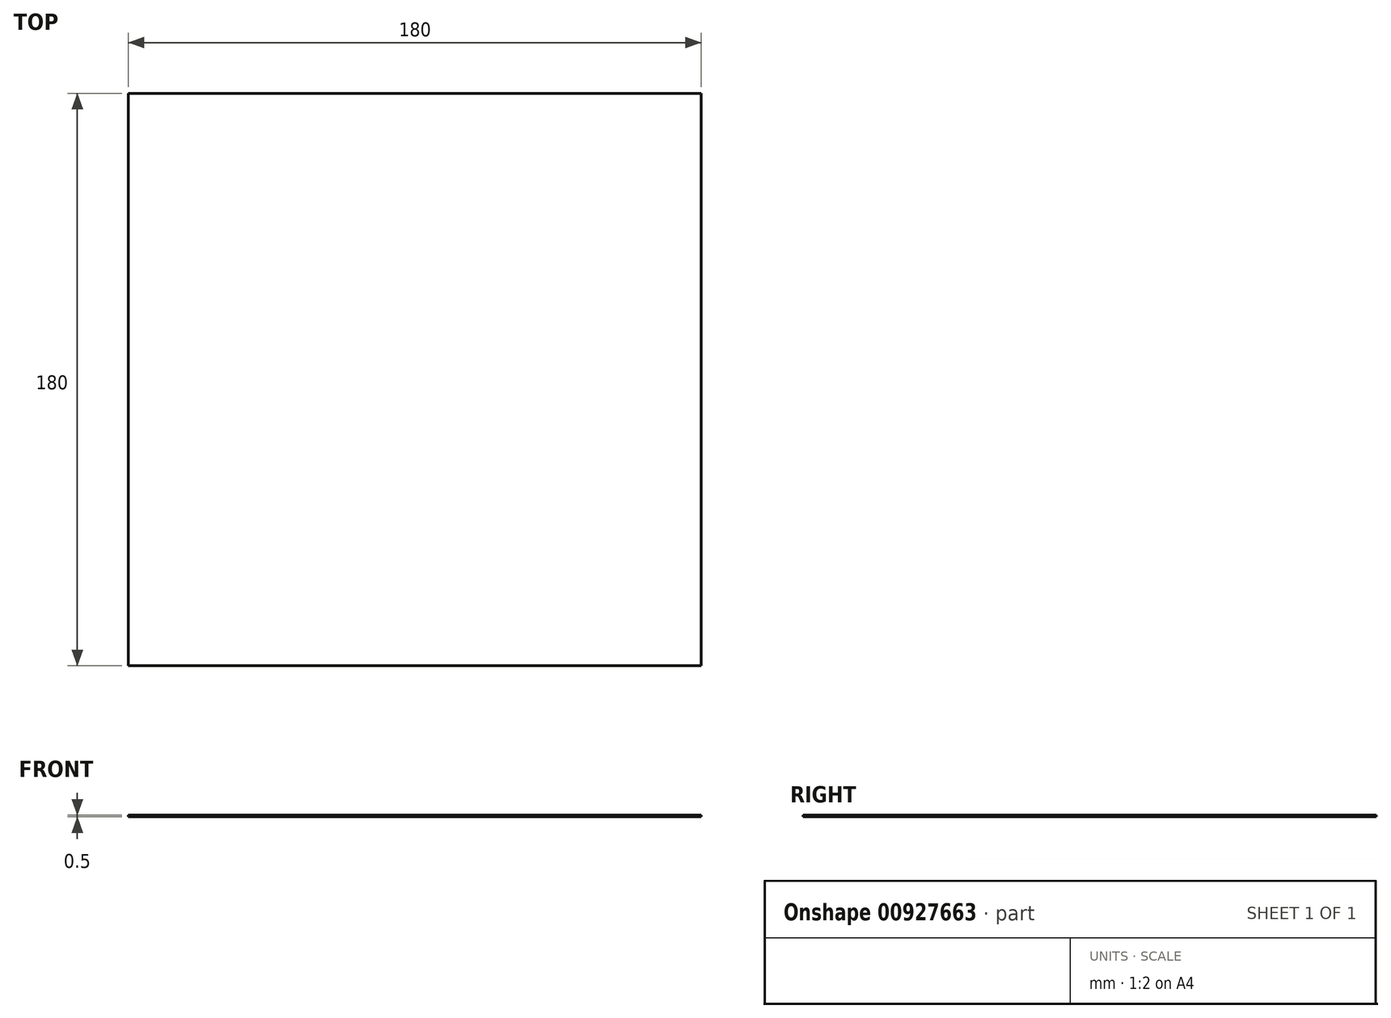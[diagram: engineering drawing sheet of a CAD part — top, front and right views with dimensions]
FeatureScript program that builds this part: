
annotation { "Feature Type Name" : "Feature", "Feature Type Description" : "" }
export const myFeature = defineFeature(function(context is Context, id is Id, definition is map)
    precondition{}
    {
        {
            var Q0;
            Q0=qCreatedBy(makeId("Top.planeOp"),FACE);
            var sketch = newSketch(context, id + "F0", { "sketchPlane" : qUnion([Q0])});
            skLineSegment(sketch, "E0.bottom", {"start": v(90, -90) * mm, "end": v(-90, -90) * mm});
            skLineSegment(sketch, "E0.top", {"start": v(90, 90) * mm, "end": v(-90, 90) * mm});
            skLineSegment(sketch, "E0.left", {"start": v(90, -90) * mm, "end": v(90, 90) * mm});
            skLineSegment(sketch, "E0.right", {"start": v(-90, -90) * mm, "end": v(-90, 90) * mm});
            skPoint(sketch, "E0.middle", {"position": v(0, 0) * mm});
            skSolve(sketch);
        }
        {
            var Q0;
            Q0=qSketchRegion(id+"F0",true);
            extrude(context, id + "F1", {"entities" : qUnion([Q0]), "depth" : 0.5 * mm, "offsetDistance" : 25 * mm});
        }
    });
